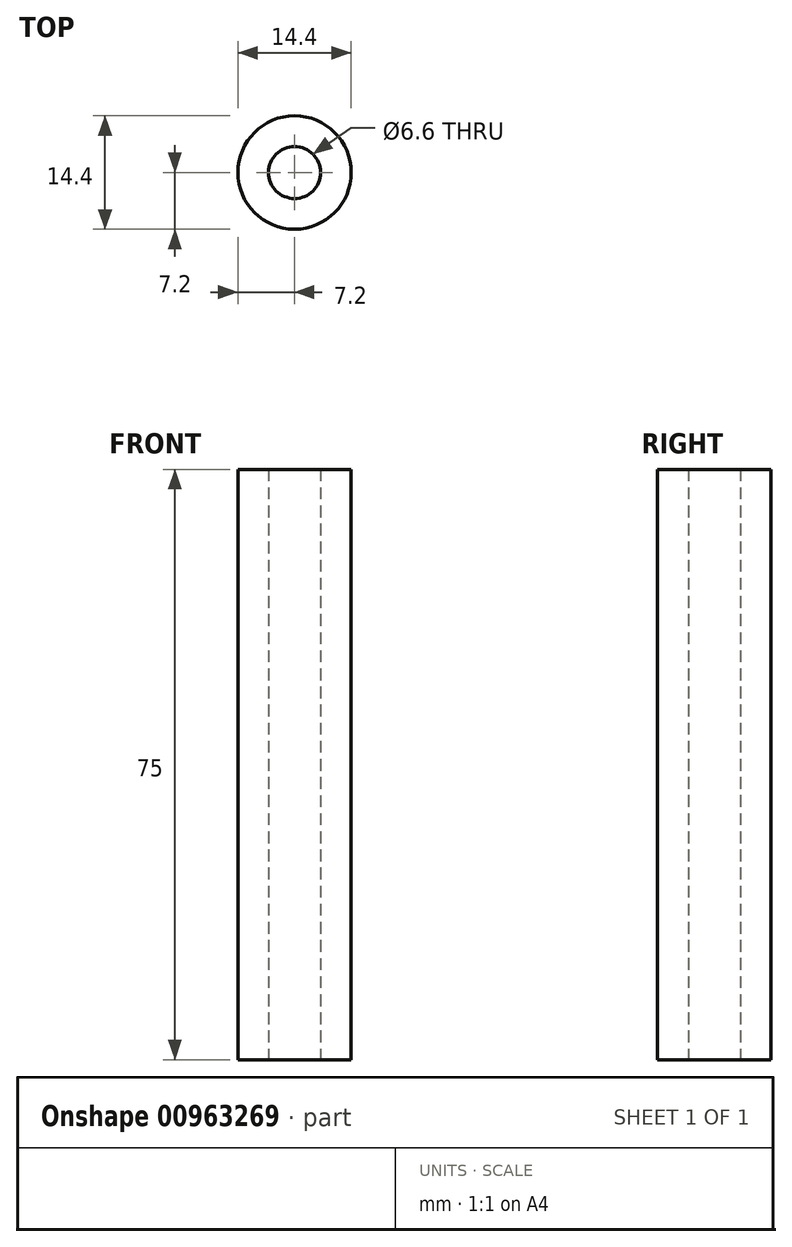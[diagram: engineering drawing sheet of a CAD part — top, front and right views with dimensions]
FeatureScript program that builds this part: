
annotation { "Feature Type Name" : "Feature", "Feature Type Description" : "" }
export const myFeature = defineFeature(function(context is Context, id is Id, definition is map)
    precondition{}
    {
        {
            var Q0;
            Q0=qCreatedBy(makeId("Top.planeOp"),FACE);
            var sketch = newSketch(context, id + "F0", { "sketchPlane" : qUnion([Q0])});
            skCircle(sketch, "E0", {"center": v(0, 0) * mm, "radius": 7.2 * mm});
            skCircle(sketch, "E1", {"center": v(0, 0) * mm, "radius": 3.3 * mm});
            skSolve(sketch);
        }
        {
            var Q0;
            Q0=makeQuery(id+"F0.imprint","IMPRINT",FACE,{"disambiguationData":[TD([[makeQuery(id+"F0.imprint","IMPRINT",EDGE,{"derivedFrom":sQuery(id+"F0.wireOp",EDGE,"E0")}),1.0]])]});
            extrude(context, id + "F1", {"entities" : qUnion([Q0]), "depth" : 75 * mm, "offsetDistance" : 25.4 * mm});
        }
    });
